# Revit family: UnoFloor Basic(Control)(Comfort)_RFA_1
name_source: partatom
category: Pipe Accessories
units: mm (PartAtom-declared; Revit-internal decimal feet)

## family parameters
Always vertical = Yes
Cut with Voids When Loaded = No
OmniClass Number = 23.65.55.14.17
OmniClass Title = Adjusting/Controlling Valves for Liquid Services
Part Type = Valve - Breaks Into
Round Connector Dimension = Use Diameter
Shared = No
Work Plane-Based = Yes

## types (6) — shared parameters
Body Material = Danfoss Steel (Zinc Plated and Painted White)
D = 20 mm  [stored 0.0656168 ft]
Default Elevation = 1219.2 mm  [stored 4 ft]
Description = Distribution Units
H = 769 mm  [stored 2.52297 ft]
H1 = 263.3 mm  [stored 0.863845 ft]
H2 = 152.6 mm  [stored 0.500656 ft]
IfcExportAs = IfcValveType
L1 = 50 mm  [stored 0.164042 ft]
L4 = 280.5 mm  [stored 0.920276 ft]
LookupTableName = Unofloor Basic(Comfort)(control)_Lookup
Manufacturer = Danfoss
Max Differential Pressure = 0.6 bar
Max Medium Temperature = 60 °C
Nominal Pressure = PN 6
Power = 0 VA
URL = https://store.danfoss.com
Voltage = 230 V
W = 111 mm

## per-type parameters (varying)
| type | IfcExportType | L2 | L3 | L5 | Left Assembly | Model | Pack Contents | Right Assembly | Type number |
| UnoFloor Control_4L-12L | Unofloor Control Left | 100.6 mm  [stored 0.330052 ft] | 189 mm  [stored 0.620079 ft] | 255.5 mm  [stored 0.838255 ft] | Yes | 088X3644,088X3645,088X3646,088X3647,088X3648,088X3650,088X3652 | Danfoss Icon2™ Master controller 230V, Actuators, Stainless steel manifold, Spacer Heat meter, AB-PM | No | 5 |
| UnoFloor Basic_4R-12R | Unofloor Basic Right | 99.6 mm  [stored 0.326772 ft] | 194 mm  [stored 0.636483 ft] | 305.5 mm  [stored 1.0023 ft] | No | 088X3124, 088X3125, 088X3126, 088X3127, 088X3128, 088X3130, 088X3132 | Danfoss Icon™ Wiring center 230V, Actuators, Stainless steel manifold, Spacer Heat meter | Yes | 2 |
| UnoFloor Basic_4L-12L | Unofloor Basic Left | 99.6 mm  [stored 0.326772 ft] | 194 mm  [stored 0.636483 ft] | 255.5 mm  [stored 0.838255 ft] | Yes | 088X3104, 088X3105, 088X3106, 088X3107, 088X3108, 088X3110, 088X3112 | Danfoss Icon™ Wiring center 230V, Actuators, Stainless steel manifold, Spacer Heat meter | No | 1 |
| UnoFloor Control_4R-12R | Unofloor Control Right | 100.6 mm  [stored 0.330052 ft] | 189 mm  [stored 0.620079 ft] | 255.5 mm  [stored 0.838255 ft] | No | 088X3664,088X3665,088X3666,088X3667,088X3668,088X3670,088X3672 | Danfoss Icon2™ Master controller 230V, Actuators, Stainless steel manifold, Spacer Heat meter, AB-PM | Yes | 6 |
| UnoFloor Comfort_2L-12L | Unofloor Comfort Left | 100.6 mm  [stored 0.330052 ft] | 189 mm  [stored 0.620079 ft] | 255.5 mm  [stored 0.838255 ft] | Yes | 088X3202,088X3203,088X3204,088X3205,088X3206,088X3207,088X3208,088X3210,088X3212 | Danfoss Icon™ Wiring center 230V, Actuators, Stainless steel manifold, Spacer Heat meter, AB-PM | No | 3 |
| UnoFloor Comfort_2R-12R | Unofloor Comfort Right | 100.6 mm  [stored 0.330052 ft] | 189 mm  [stored 0.620079 ft] | 255.5 mm  [stored 0.838255 ft] | No | 088X3222,088X3223,088X3224,088X3225,088X3226,088X3227,088X3228,088X3230,088X3232 | Danfoss Icon™ Wiring center 230V, Actuators, Stainless steel manifold, Spacer Heat meter, AB-PM | Yes | 4 |

note: [stored X ft] marks values corroborated as IEEE doubles in the binary element streams (Revit-internal decimal feet)

## geometry (parser evidence)
native form markers: Sweep x1
no freeform markers — native parametric forms only
